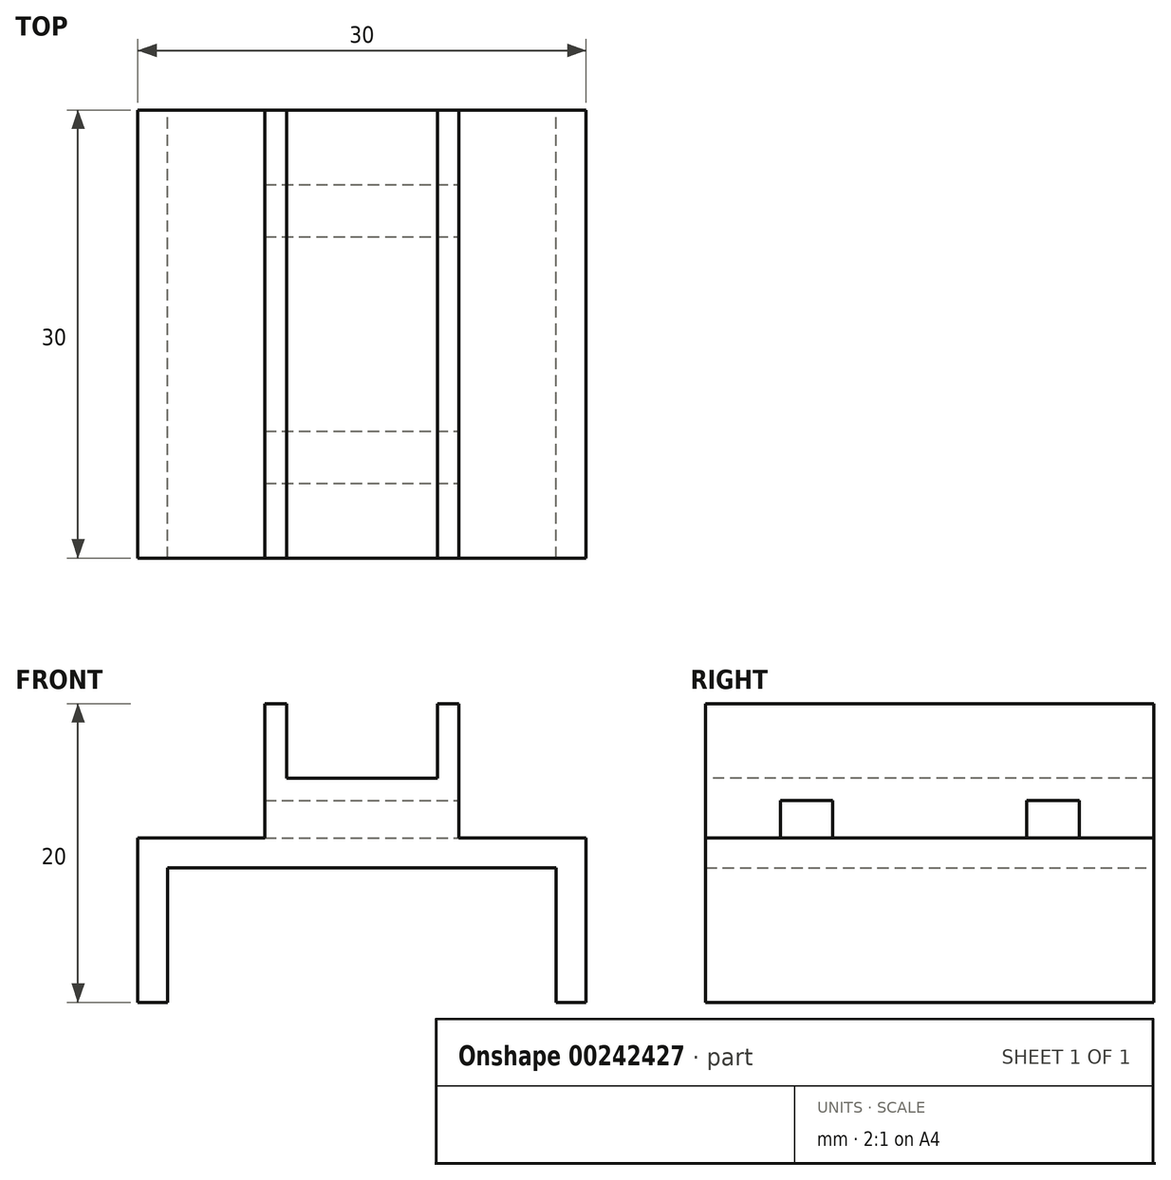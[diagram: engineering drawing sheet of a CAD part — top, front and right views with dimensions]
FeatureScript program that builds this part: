
annotation { "Feature Type Name" : "Feature", "Feature Type Description" : "" }
export const myFeature = defineFeature(function(context is Context, id is Id, definition is map)
    precondition{}
    {
        {
            var Q0;
            Q0=qCreatedBy(makeId("Top.planeOp"),FACE);
            var sketch = newSketch(context, id + "F0", { "sketchPlane" : qUnion([Q0])});
            skLineSegment(sketch, "E0.bottom", {"start": v(15, -15) * mm, "end": v(-15, -15) * mm});
            skLineSegment(sketch, "E0.top", {"start": v(15, 15) * mm, "end": v(-15, 15) * mm});
            skLineSegment(sketch, "E0.left", {"start": v(15, -15) * mm, "end": v(15, 15) * mm});
            skLineSegment(sketch, "E0.right", {"start": v(-15, -15) * mm, "end": v(-15, 15) * mm});
            skPoint(sketch, "E0.middle", {"position": v(0, 0) * mm});
            skSolve(sketch);
        }
        {
            var Q0;
            Q0=makeQuery(id+"F0.imprint","IMPRINT",FACE,{"disambiguationData":[TD([[makeQuery(id+"F0.imprint","IMPRINT",EDGE,{"derivedFrom":sQuery(id+"F0.wireOp",EDGE,"E0.bottom")}),-1.0]])]});
            extrude(context, id + "F1", {"entities" : qUnion([Q0]), "depth" : 11 * mm, "offsetDistance" : 25 * mm});
        }
        {
            var Q0;
            Q0=makeQuery(id+"F1.opExtrude","CAP_FACE",FACE,{"disambiguationData":[OSD([sQuery(id+"F0.wireOp",EDGE,"E0.bottom"),sQuery(id+"F0.wireOp",EDGE,"E0.top"),sQuery(id+"F0.wireOp",EDGE,"E0.left"),sQuery(id+"F0.wireOp",EDGE,"E0.right")])],"isStart":true});
            var sketch = newSketch(context, id + "F2", { "sketchPlane" : qUnion([Q0])});
            skLineSegment(sketch, "E1", {"start": v(-13, 15) * mm, "end": v(-13, -15) * mm});
            skLineSegment(sketch, "E2", {"start": v(13, 15) * mm, "end": v(13, -15) * mm});
            skLineSegment(sketch, "E3", {"start": v(0, -19.21) * mm, "end": v(0, -15) * mm, "construction": true});
            skSolve(sketch);
        }
        {
            var Q0;
            {var subQ0=sQuery(id+"F2.wireOp",EDGE,"E1");Q0=makeQuery(id+"F2.imprint","IMPRINT",FACE,{"disambiguationData":[TD([[makeQuery(id+"F2.imprint","IMPRINT",EDGE,{"derivedFrom":subQ0}),1.0]])]});}
            extrude(context, id + "F3", {"entities" : qUnion([Q0]), "operationType" : NewBodyOperationType.REMOVE, "oppositeDirection" : true, "depth" : 9 * mm, "offsetDistance" : 25 * mm});
        }
        {
            var Q0;
            Q0=makeQuery(id+"F1.opExtrude","CAP_FACE",FACE,{"disambiguationData":[OSD([sQuery(id+"F0.wireOp",EDGE,"E0.bottom"),sQuery(id+"F0.wireOp",EDGE,"E0.top"),sQuery(id+"F0.wireOp",EDGE,"E0.left"),sQuery(id+"F0.wireOp",EDGE,"E0.right")])],"isStart":false});
            var sketch = newSketch(context, id + "F4", { "sketchPlane" : qUnion([Q0])});
            skLineSegment(sketch, "E4", {"start": v(-6.5, 15) * mm, "end": v(-6.5, -15) * mm});
            skLineSegment(sketch, "E5", {"start": v(6.5, 15) * mm, "end": v(6.5, -15) * mm});
            skLineSegment(sketch, "E6", {"start": v(-5.05, 15) * mm, "end": v(-5.05, -15) * mm});
            skLineSegment(sketch, "E7", {"start": v(5.05, 15) * mm, "end": v(5.05, -15) * mm});
            skSolve(sketch);
        }
        {
            var Q0;
            {var subQ0=sQuery(id+"F4.wireOp",EDGE,"E4");Q0=makeQuery(id+"F4.imprint","IMPRINT",FACE,{"disambiguationData":[TD([[makeQuery(id+"F4.imprint","IMPRINT",EDGE,{"derivedFrom":subQ0}),1.0]])]});}
            var Q1;
            {var subQ0=sQuery(id+"F4.wireOp",EDGE,"E5");Q1=makeQuery(id+"F4.imprint","IMPRINT",FACE,{"disambiguationData":[TD([[makeQuery(id+"F4.imprint","IMPRINT",EDGE,{"derivedFrom":subQ0}),-1.0]])]});}
            extrude(context, id + "F5", {"entities" : qUnion([Q0, Q1]), "operationType" : NewBodyOperationType.ADD, "depth" : 9 * mm, "offsetDistance" : 25 * mm});
        }
        {
            var Q0;
            {var subQ1=sQuery(id+"F4.wireOp",EDGE,"E6");var subQ2=sQuery(id+"F0.wireOp",EDGE,"E0.top");var subQ4=sQuery(id+"F0.wireOp",EDGE,"E0.bottom");Q0=makeQuery(id+"F5.boolean.opBoolean","SPLIT",FACE,{"disambiguationData":[TD([makeQuery(id+"F5.opExtrude","SWEPT_FACE",FACE,{"disambiguationData":[OSD([subQ1])]})])],"derivedFrom":makeQuery(id+"F1.opExtrude","CAP_FACE",FACE,{"disambiguationData":[OSD([subQ4,subQ2,sQuery(id+"F0.wireOp",EDGE,"E0.left"),sQuery(id+"F0.wireOp",EDGE,"E0.right")])],"isStart":false})});}
            extrude(context, id + "F6", {"entities" : qUnion([Q0]), "operationType" : NewBodyOperationType.ADD, "depth" : 4 * mm, "offsetDistance" : 25 * mm});
        }
        {
            var Q0;
            Q0=makeQuery(id+"F5.opExtrude","SWEPT_FACE",FACE,{"disambiguationData":[OSD([sQuery(id+"F4.wireOp",EDGE,"E5")])]});
            var sketch = newSketch(context, id + "F7", { "sketchPlane" : qUnion([Q0])});
            skLineSegment(sketch, "E8.bottom", {"start": v(-6.5, 11) * mm, "end": v(-10, 11) * mm});
            skLineSegment(sketch, "E8.top", {"start": v(-6.5, 13.5) * mm, "end": v(-10, 13.5) * mm});
            skLineSegment(sketch, "E8.left", {"start": v(-6.5, 11) * mm, "end": v(-6.5, 13.5) * mm});
            skLineSegment(sketch, "E8.right", {"start": v(-10, 11) * mm, "end": v(-10, 13.5) * mm});
            skPoint(sketch, "E8.middle", {"position": v(-8.25, 12.25) * mm});
            skLineSegment(sketch, "E9.bottom", {"start": v(10, 11) * mm, "end": v(6.5, 11) * mm});
            skLineSegment(sketch, "E9.top", {"start": v(10, 13.5) * mm, "end": v(6.5, 13.5) * mm});
            skLineSegment(sketch, "E9.left", {"start": v(10, 11) * mm, "end": v(10, 13.5) * mm});
            skLineSegment(sketch, "E9.right", {"start": v(6.5, 11) * mm, "end": v(6.5, 13.5) * mm});
            skPoint(sketch, "E9.middle", {"position": v(8.25, 12.25) * mm});
            skLineSegment(sketch, "E10", {"start": v(0, 11) * mm, "end": v(0, 15.59) * mm, "construction": true});
            skSolve(sketch);
        }
        {
            var Q0;
            Q0=makeQuery(id+"F7.imprint","IMPRINT",FACE,{"disambiguationData":[TD([[makeQuery(id+"F7.imprint","IMPRINT",EDGE,{"derivedFrom":sQuery(id+"F7.wireOp",EDGE,"E8.bottom")}),-1.0]])]});
            var Q1;
            Q1=makeQuery(id+"F7.imprint","IMPRINT",FACE,{"disambiguationData":[TD([[makeQuery(id+"F7.imprint","IMPRINT",EDGE,{"derivedFrom":sQuery(id+"F7.wireOp",EDGE,"E9.bottom")}),-1.0]])]});
            extrude(context, id + "F8", {"entities" : qUnion([Q0, Q1]), "operationType" : NewBodyOperationType.REMOVE, "endBound" : BoundingType.UP_TO_NEXT, "oppositeDirection" : true, "depth" : 25 * mm, "offsetDistance" : 25 * mm});
        }
    });
